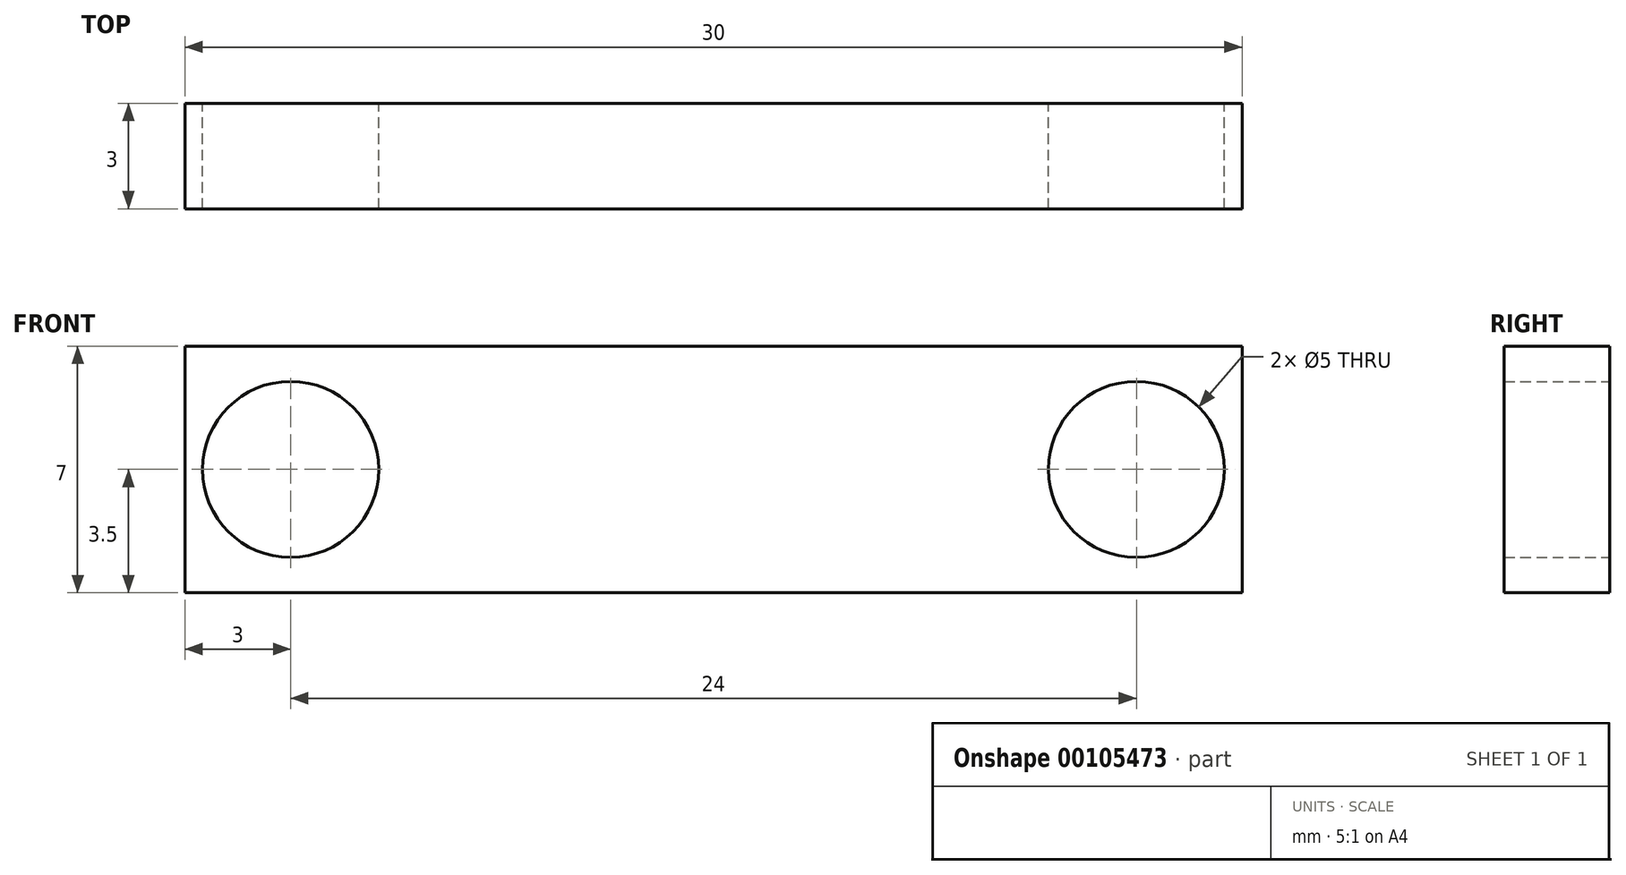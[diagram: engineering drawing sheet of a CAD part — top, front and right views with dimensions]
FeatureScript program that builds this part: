
annotation { "Feature Type Name" : "Feature", "Feature Type Description" : "" }
export const myFeature = defineFeature(function(context is Context, id is Id, definition is map)
    precondition{}
    {
        {
            var Q0;
            Q0=qCreatedBy(makeId("Front.planeOp"),FACE);
            var sketch = newSketch(context, id + "F0", { "sketchPlane" : qUnion([Q0])});
            skLineSegment(sketch, "E0.bottom", {"start": v(0, 0) * mm, "end": v(30, 0) * mm});
            skLineSegment(sketch, "E0.top", {"start": v(0, -7) * mm, "end": v(30, -7) * mm});
            skLineSegment(sketch, "E0.left", {"start": v(0, 0) * mm, "end": v(0, -7) * mm});
            skLineSegment(sketch, "E0.right", {"start": v(30, 0) * mm, "end": v(30, -7) * mm});
            skCircle(sketch, "E1", {"center": v(3, -3.5) * mm, "radius": 2.5 * mm});
            skPoint(sketch, "E1.centerSnap0", {"position": v(0, -3.5) * mm});
            skCircle(sketch, "E2", {"center": v(27, -3.5) * mm, "radius": 2.5 * mm});
            skPoint(sketch, "E2.centerSnap0", {"position": v(30, -3.5) * mm});
            skSolve(sketch);
        }
        {
            var Q0;
            Q0 = qSketchRegion(id + "F0", true);
            extrude(context, id + "F1", {"entities" : qUnion([Q0]), "depth" : 3 * mm});
        }
    });
